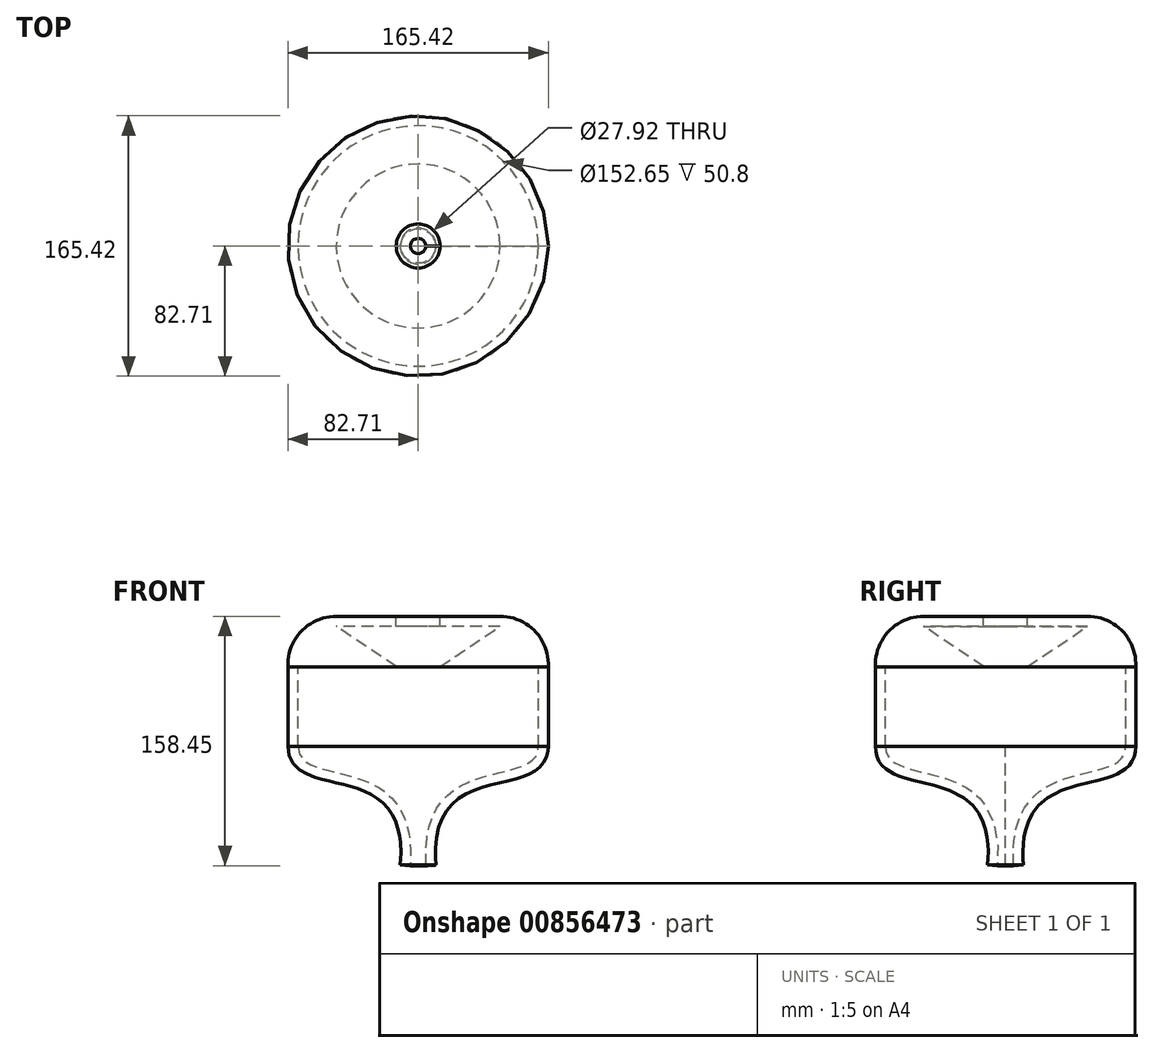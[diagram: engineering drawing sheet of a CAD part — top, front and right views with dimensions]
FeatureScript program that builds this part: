
annotation { "Feature Type Name" : "Feature", "Feature Type Description" : "" }
export const myFeature = defineFeature(function(context is Context, id is Id, definition is map)
    precondition{}
    {
        {
            var Q0;
            Q0=qCreatedBy(makeId("Front.planeOp"),FACE);
            var sketch = newSketch(context, id + "F0", { "sketchPlane" : qUnion([Q0])});
            skLineSegment(sketch, "E0", {"start": v(0, 76.66) * mm, "end": v(0, -75.74) * mm, "construction": true});
            skLineSegment(sketch, "E1", {"start": v(13.96, 76.36) * mm, "end": v(52.06, 76.36) * mm});
            skLineSegment(sketch, "E2", {"start": v(76.32, 0) * mm, "end": v(76.32, 50.8) * mm});
            skArc(sketch, "E3", {"start": v(76.32, 50.8) * mm, "mid": v(69.68, 68.8) * mm, "end": v(52.06, 76.36) * mm});
            skFitSpline(sketch, "E4", {"points": [v(5.08, -75.74) * mm, v(76.32, 0) * mm], "startDerivative": vector(-15.24, 227.22) * mm, "endDerivative": vector(0, 84.6) * mm});
            skLineSegment(sketch, "E5.0", {"start": v(13.96, 82.71) * mm, "end": v(52.06, 82.71) * mm});
            skArc(sketch, "E5.1", {"start": v(82.67, 50.64) * mm, "mid": v(74.23, 73.23) * mm, "end": v(52.06, 82.71) * mm});
            skLineSegment(sketch, "E5.2", {"start": v(82.67, 0) * mm, "end": v(82.67, 50.64) * mm});
            skFitSpline(sketch, "E5.3", {"points": [v(11.42, -75.32) * mm, v(11.12, -70.84) * mm, v(11.12, -62.77) * mm, v(12.65, -53.06) * mm, v(15.36, -45.46) * mm, v(18.99, -39.56) * mm, v(23.4, -34.93) * mm, v(28.55, -31.24) * mm, v(34.38, -28.32) * mm, v(40.7, -26.01) * mm, v(47.3, -24.16) * mm, v(53.95, -22.56) * mm, v(60.46, -20.98) * mm, v(65.63, -19.47) * mm, v(69.56, -17.95) * mm, v(72.4, -16.59) * mm, v(75.1, -14.91) * mm, v(77.6, -12.82) * mm, v(79.78, -10.23) * mm, v(81.45, -7.13) * mm, v(82.46, -3.68) * mm, v(82.67, -1.24) * mm, v(82.67, 0) * mm]});
            skLineSegment(sketch, "E6", {"start": v(13.96, 82.71) * mm, "end": v(13.96, 76.36) * mm});
            skLineSegment(sketch, "E7", {"start": v(5.08, -75.74) * mm, "end": v(11.42, -75.32) * mm});
            skLineSegment(sketch, "E8", {"start": v(76.32, 50.8) * mm, "end": v(13.96, 50.8) * mm});
            skLineSegment(sketch, "E9", {"start": v(13.96, 50.8) * mm, "end": v(52.06, 76.36) * mm});
            skSolve(sketch);
        }
        {
            var Q0;
            Q0 = qSketchRegion(id + "F0", true);
            var Q1;
            Q1=sQuery(id+"F0.wireOp",EDGE,"E0");
            revolve(context, id + "F1", {"surfaceOperationType" : NewSurfaceOperationType.NEW, "entities" : qUnion([Q0]), "axis" : qUnion([Q1]), "revolveType" : RevolveType.FULL});
        }
    });
